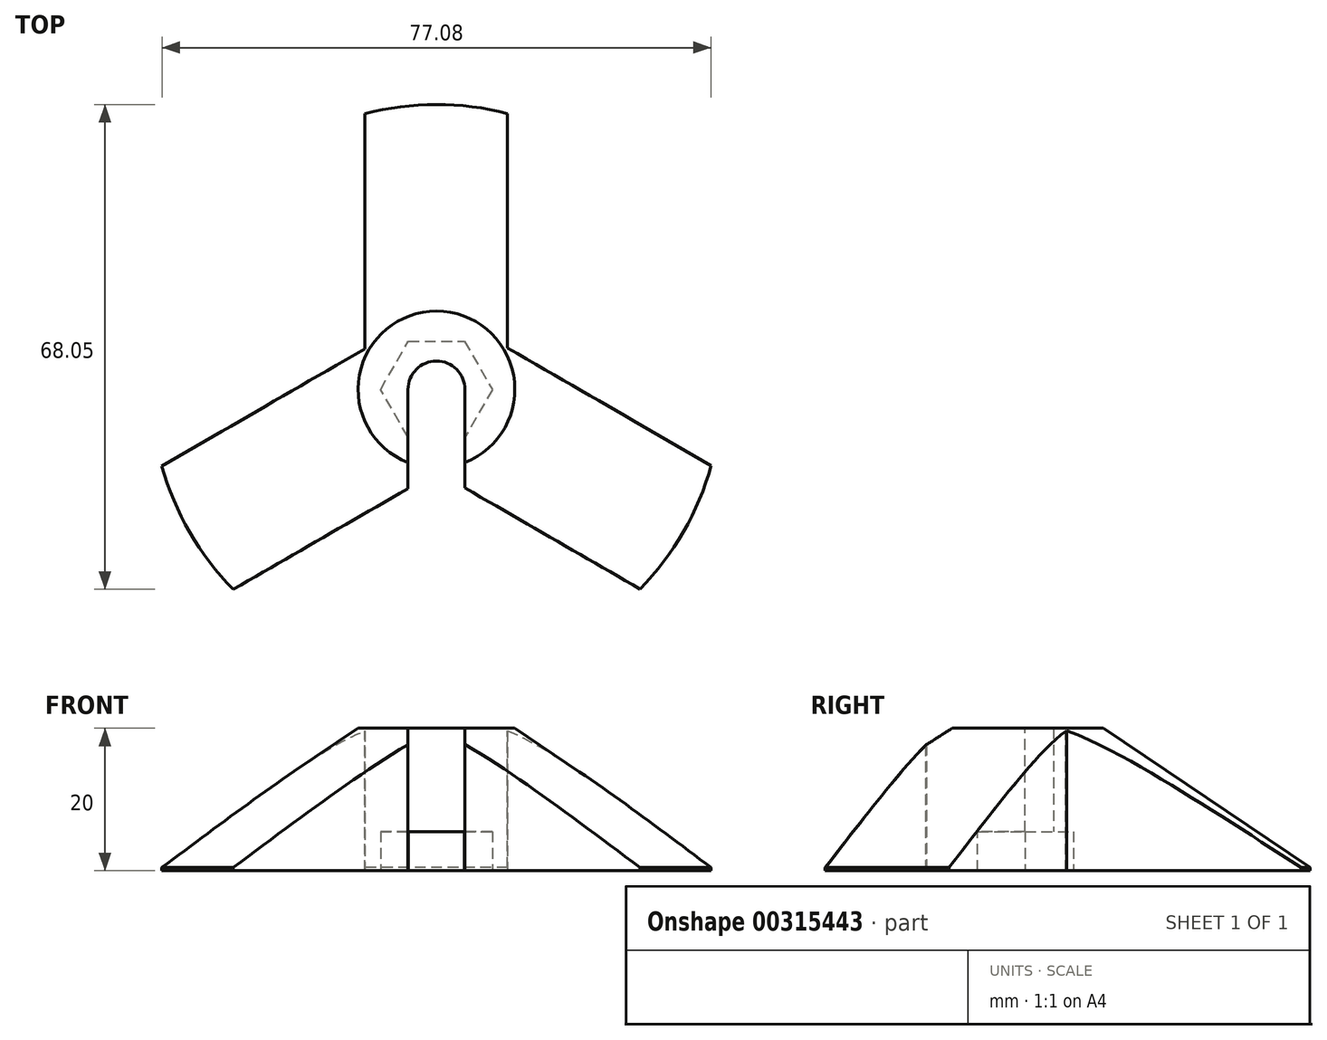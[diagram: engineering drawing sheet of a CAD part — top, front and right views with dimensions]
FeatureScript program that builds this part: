
annotation { "Feature Type Name" : "Feature", "Feature Type Description" : "" }
export const myFeature = defineFeature(function(context is Context, id is Id, definition is map)
    precondition{}
    {
        {
            var Q0;
            Q0=qCreatedBy(makeId("Top.planeOp"),FACE);
            var sketch = newSketch(context, id + "F0", { "sketchPlane" : qUnion([Q0])});
            skCircle(sketch, "E0", {"center": v(0, 0) * mm, "radius": 4 * mm});
            skLineSegment(sketch, "E1.bottom", {"start": v(9.97, 0) * mm, "end": v(-10.03, 0) * mm});
            skLineSegment(sketch, "E1.top", {"start": v(9.97, 40) * mm, "end": v(-10.03, 40) * mm});
            skLineSegment(sketch, "E1.left", {"start": v(9.97, 0) * mm, "end": v(9.97, 40) * mm});
            skLineSegment(sketch, "E1.right", {"start": v(-10.03, 0) * mm, "end": v(-10.03, 40) * mm});
            skCircle(sketch, "E2", {"center": v(0, 0) * mm, "radius": 40 * mm});
            skCircle(sketch, "E3.cCircle", {"center": v(0, 0) * mm, "radius": 7.85 * mm, "construction": true});
            skLineSegment(sketch, "E3.0", {"start": v(-7.85, 0) * mm, "end": v(-3.93, 6.8) * mm});
            skLineSegment(sketch, "E3.1", {"start": v(-3.93, 6.8) * mm, "end": v(3.93, 6.8) * mm});
            skLineSegment(sketch, "E3.2", {"start": v(3.93, 6.8) * mm, "end": v(7.85, 0) * mm});
            skLineSegment(sketch, "E3.3", {"start": v(7.85, 0) * mm, "end": v(3.93, -6.8) * mm});
            skLineSegment(sketch, "E3.4", {"start": v(3.93, -6.8) * mm, "end": v(-3.93, -6.8) * mm});
            skLineSegment(sketch, "E3.5", {"start": v(-3.93, -6.8) * mm, "end": v(-7.85, 0) * mm});
            skSolve(sketch);
        }
        {
            var Q0;
            {var subQ1=sQuery(id+"F0.wireOp",EDGE,"E1.bottom");var subQ3=sQuery(id+"F0.wireOp",EDGE,"E0");var subQ9=makeQuery(id+"F0.imprint","INTERSECT",VERTEX,{"disambiguationData":[OD(0.0)],"derivedFrom":[subQ3,subQ1]});Q0=makeQuery(id+"F0.imprint","IMPRINT",FACE,{"disambiguationData":[TD([[makeQuery(id+"F0.imprint","IMPRINT",EDGE,{"disambiguationData":[TD([[subQ9,-1.0]])],"derivedFrom":subQ3}),-1.0]])]});}
            var Q1;
            {var subQ10=sQuery(id+"F0.wireOp",EDGE,"E3.1");Q1=makeQuery(id+"F0.imprint","IMPRINT",FACE,{"disambiguationData":[TD([[makeQuery(id+"F0.imprint","IMPRINT",EDGE,{"derivedFrom":subQ10}),1.0]])]});}
            extrude(context, id + "F1", {"entities" : qUnion([Q0, Q1]), "depth" : 20 * mm});
        }
        {
            var Q0;
            {var subQ0=sQuery(id+"F0.wireOp",EDGE,"E3.3");Q0=makeQuery(id+"F0.imprint","IMPRINT",FACE,{"disambiguationData":[TD([[makeQuery(id+"F0.imprint","IMPRINT",EDGE,{"derivedFrom":subQ0}),-1.0]])]});}
            var Q1;
            {var subQ0=sQuery(id+"F0.wireOp",EDGE,"E3.0");Q1=makeQuery(id+"F0.imprint","IMPRINT",FACE,{"disambiguationData":[TD([[makeQuery(id+"F0.imprint","IMPRINT",EDGE,{"derivedFrom":subQ0}),-1.0]])]});}
            extrude(context, id + "F2", {"entities" : qUnion([Q0, Q1]), "operationType" : NewBodyOperationType.REMOVE, "depth" : 5.5 * mm});
        }
        {
            var Q0;
            Q0=makeQuery(id+"F1.opExtrude","CAP_EDGE",EDGE,{"disambiguationData":[OSD([sQuery(id+"F0.wireOp",EDGE,"E2")])],"isStart":false});
            chamfer(context, id + "F3", {"entities" : qUnion([Q0]), "chamferType" : ChamferType.OFFSET_ANGLE, "width" : 29 * mm, "oppositeDirection" : false, "angle" : 34 * degree, "tangentPropagation" : true});
        }
        {
            var Q0;
            Q0=makeQuery(id+"F1.opExtrude","SWEPT_BODY",BODY,{"disambiguationData":[OSD([sQuery(id+"F0.wireOp",EDGE,"E0"),sQuery(id+"F0.wireOp",EDGE,"E1.bottom"),sQuery(id+"F0.wireOp",EDGE,"E1.left"),sQuery(id+"F0.wireOp",EDGE,"E1.right"),sQuery(id+"F0.wireOp",EDGE,"E2")])]});
            var Q1;
            Q1=makeQuery(id+"F3.opChamfer","BLEND_FACE",FACE,{"disambiguationData":[OSD([sQuery(id+"F0.wireOp",EDGE,"E2")])]});
            circularPattern(context, id + "F4", {"operationType" : NewBodyOperationType.ADD, "entities" : qUnion([Q0]), "axis" : qUnion([Q1]), "angle" : 360 * degree, "instanceCount" : 3, "equalSpace" : true});
        }
        {
            var Q0;
            {var subQ0=makeQuery(id+"F1.opExtrude","CAP_FACE",FACE,{"disambiguationData":[OSD([sQuery(id+"F0.wireOp",EDGE,"E0"),sQuery(id+"F0.wireOp",EDGE,"E1.bottom"),sQuery(id+"F0.wireOp",EDGE,"E1.left"),sQuery(id+"F0.wireOp",EDGE,"E1.right"),sQuery(id+"F0.wireOp",EDGE,"E2")])],"isStart":false});Q0=makeQuery(id+"F4.boolean.opBoolean","MERGE",FACE,{"derivedFrom":[subQ0,makeQuery(id+"F4.opPattern","COPY",FACE,{"derivedFrom":subQ0,"instanceName":"1"}),makeQuery(id+"F4.opPattern","COPY",FACE,{"derivedFrom":subQ0,"instanceName":"2"})]});}
            var sketch = newSketch(context, id + "F5", { "sketchPlane" : qUnion([Q0])});
            skCircle(sketch, "E4.0", {"center": v(0, 0) * mm, "radius": 4 * mm});
            skLineSegment(sketch, "E5.bottom", {"start": v(4, 0) * mm, "end": v(-4.02, 0) * mm});
            skLineSegment(sketch, "E5.top", {"start": v(4, -15.1) * mm, "end": v(-4.02, -15.1) * mm});
            skLineSegment(sketch, "E5.left", {"start": v(4, 0) * mm, "end": v(4, -15.1) * mm});
            skLineSegment(sketch, "E5.right", {"start": v(-4.02, 0) * mm, "end": v(-4.02, -15.1) * mm});
            skSolve(sketch);
        }
        {
            var Q0;
            {var subQ0=sQuery(id+"F5.wireOp",EDGE,"E5.right");var subQ1=sQuery(id+"F5.wireOp",EDGE,"E5.bottom");var subQ2=makeQuery(id+"F5.imprint","INTERSECT",VERTEX,{"derivedFrom":[subQ1,subQ0]});Q0=makeQuery(id+"F5.imprint","IMPRINT",FACE,{"disambiguationData":[TD([[makeQuery(id+"F5.imprint","IMPRINT",EDGE,{"disambiguationData":[TD([[subQ2,1.0]])],"derivedFrom":subQ1}),1.0]])]});}
            var Q1;
            {var subQ0=sQuery(id+"F5.wireOp",EDGE,"E5.top");Q1=makeQuery(id+"F5.imprint","IMPRINT",FACE,{"disambiguationData":[TD([[makeQuery(id+"F5.imprint","IMPRINT",EDGE,{"derivedFrom":subQ0}),-1.0]])]});}
            extrude(context, id + "F6", {"entities" : qUnion([Q0, Q1]), "operationType" : NewBodyOperationType.REMOVE, "endBound" : BoundingType.UP_TO_NEXT, "oppositeDirection" : true, "depth" : 25 * mm});
        }
    });
